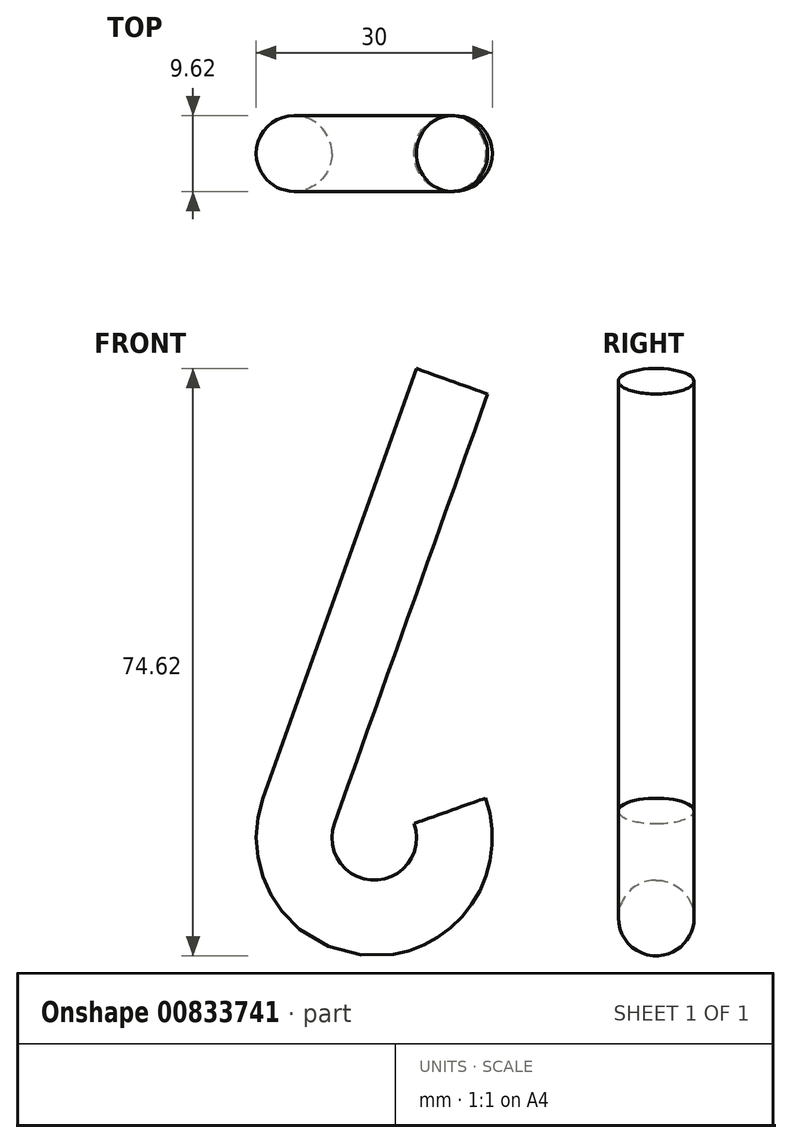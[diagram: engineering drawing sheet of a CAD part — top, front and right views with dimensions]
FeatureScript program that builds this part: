
annotation { "Feature Type Name" : "Feature", "Feature Type Description" : "" }
export const myFeature = defineFeature(function(context is Context, id is Id, definition is map)
    precondition{}
    {
        {
            var Q0;
            Q0=qCreatedBy(makeId("Front.planeOp"),FACE);
            var sketch = newSketch(context, id + "F0", { "sketchPlane" : qUnion([Q0])});
            skArc(sketch, "E0", {"start": v(-9.42, 3.36) * mm, "mid": v(0, -10) * mm, "end": v(9.42, 3.36) * mm});
            skArc(sketch, "E1", {"start": v(9.42, 56.18) * mm, "mid": v(0.9, 69.5) * mm, "end": v(-9.87, 57.94) * mm});
            skLineSegment(sketch, "E2", {"start": v(10.05, 57.94) * mm, "end": v(-9.42, 3.36) * mm});
            skLineSegment(sketch, "E3", {"start": v(10.05, 57.94) * mm, "end": v(-33.15, 57.94) * mm, "construction": true});
            skLineSegment(sketch, "E4", {"start": v(-9.42, 3.36) * mm, "end": v(38.97, 3.36) * mm, "construction": true});
            skPoint(sketch, "E5", {"position": v(-10, 0) * mm});
            skSolve(sketch);
        }
        {
            var Q0;
            Q0=qCreatedBy(makeId("Top.planeOp"),FACE);
            var sketch = newSketch(context, id + "F1", { "sketchPlane" : qUnion([Q0])});
            skCircle(sketch, "E6", {"center": v(-10.19, 0) * mm, "radius": 4.8 * mm});
            skSolve(sketch);
        }
        {
            var Q0;
            Q0=makeQuery(id+"F1.imprint","IMPRINT",FACE,{"disambiguationData":[TD([[makeQuery(id+"F1.imprint","IMPRINT",EDGE,{"derivedFrom":sQuery(id+"F1.wireOp",EDGE,"E6")}),1.0]])]});
            var Q1;
            Q1=sQuery(id+"F0.wireOp",EDGE,"E2");
            var Q2;
            Q2=sQuery(id+"F0.wireOp",EDGE,"E0");
            sweep(context, id + "F2", {"profiles" : qUnion([Q0]), "path" : qUnion([Q1, Q2])});
        }
    });
